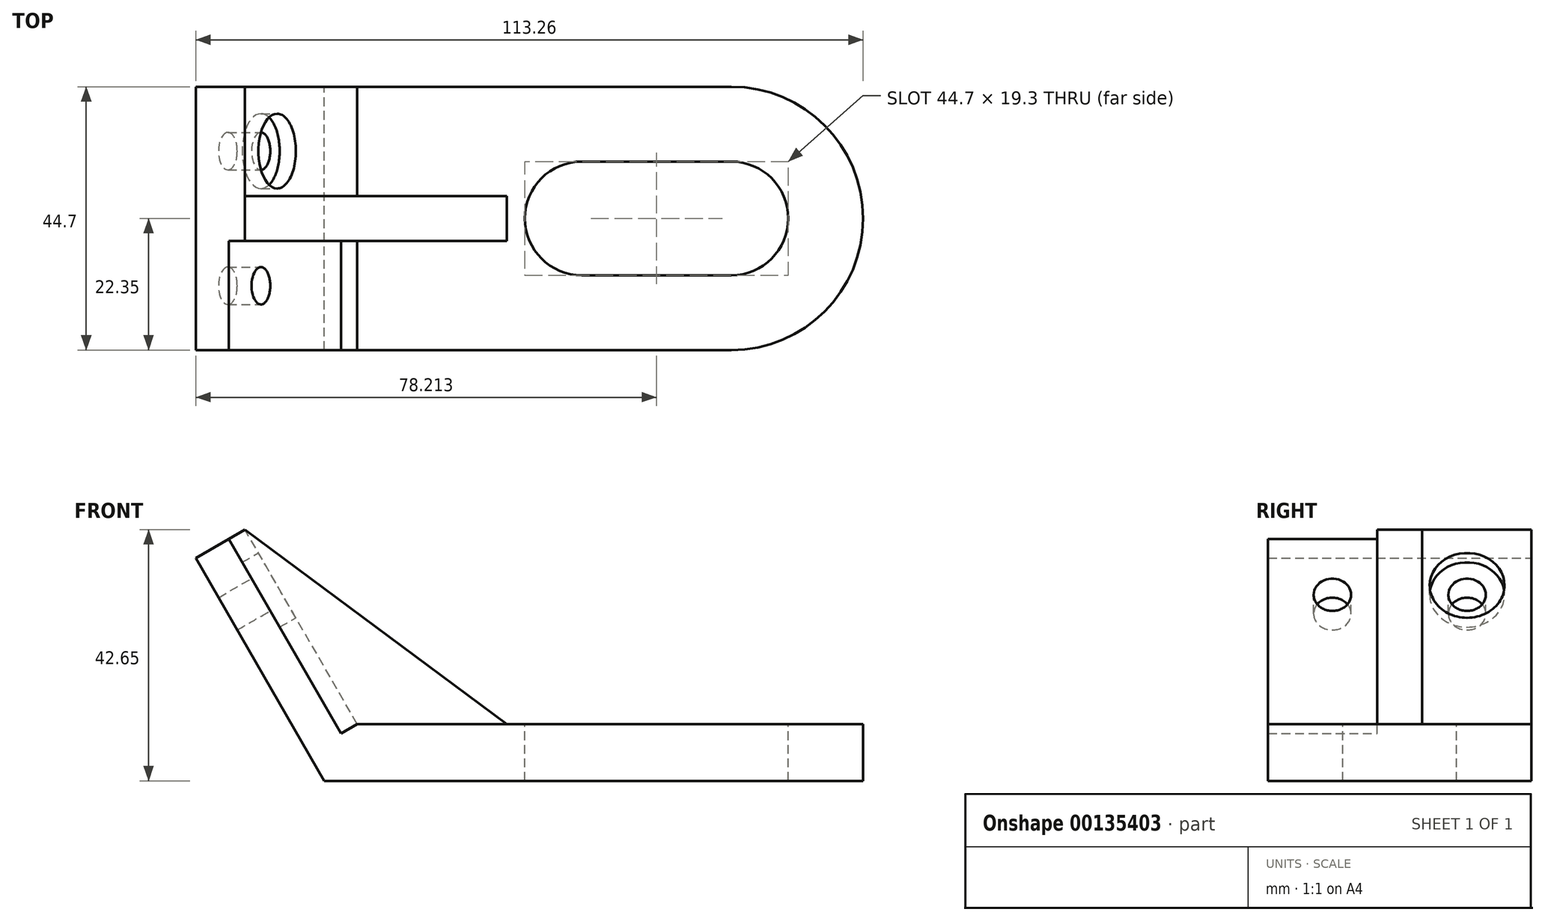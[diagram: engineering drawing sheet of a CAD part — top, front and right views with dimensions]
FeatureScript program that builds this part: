
annotation { "Feature Type Name" : "Feature", "Feature Type Description" : "" }
export const myFeature = defineFeature(function(context is Context, id is Id, definition is map)
    precondition{}
    {
        {
            var Q0;
            Q0=qCreatedBy(makeId("Front.planeOp"),FACE);
            var sketch = newSketch(context, id + "F0", { "sketchPlane" : qUnion([Q0])});
            skLineSegment(sketch, "E0", {"start": v(-21.84, 37.82) * mm, "end": v(0, 0) * mm});
            skLineSegment(sketch, "E1", {"start": v(0, 0) * mm, "end": v(91.42, 0) * mm});
            skLineSegment(sketch, "E2", {"start": v(91.42, 0) * mm, "end": v(91.42, 9.65) * mm});
            skLineSegment(sketch, "E3", {"start": v(91.42, 9.65) * mm, "end": v(5.57, 9.65) * mm});
            skLineSegment(sketch, "E4", {"start": v(5.57, 9.65) * mm, "end": v(-13.48, 42.65) * mm});
            skLineSegment(sketch, "E5", {"start": v(-13.48, 42.65) * mm, "end": v(-21.84, 37.82) * mm});
            skLineSegment(sketch, "E6", {"start": v(-13.48, 42.65) * mm, "end": v(30.97, 9.65) * mm});
            skLineSegment(sketch, "E7", {"start": v(-21.84, 37.82) * mm, "end": v(-21.84, 0) * mm, "construction": true});
            skSolve(sketch);
        }
        {
            var Q0;
            Q0=makeQuery(id+"F0.imprint","IMPRINT",FACE,{"disambiguationData":[TD([[makeQuery(id+"F0.imprint","IMPRINT",EDGE,{"derivedFrom":sQuery(id+"F0.wireOp",EDGE,"E0")}),1.0]])]});
            extrude(context, id + "F1", {"entities" : qUnion([Q0]), "endBound" : BoundingType.SYMMETRIC, "depth" : 44.7 * mm});
        }
        {
            var Q0;
            {var subQ0=sQuery(id+"F0.wireOp",EDGE,"E4");Q0=makeQuery(id+"F0.imprint","IMPRINT",FACE,{"disambiguationData":[TD([[makeQuery(id+"F0.imprint","IMPRINT",EDGE,{"derivedFrom":subQ0}),-1.0]])]});}
            extrude(context, id + "F2", {"entities" : qUnion([Q0]), "operationType" : NewBodyOperationType.ADD, "endBound" : BoundingType.SYMMETRIC, "depth" : 7.62 * mm});
        }
        {
            var Q0;
            Q0=makeQuery(id+"F1.opExtrude","SWEPT_FACE",FACE,{"disambiguationData":[OSD([sQuery(id+"F0.wireOp",EDGE,"E3")])]});
            var sketch = newSketch(context, id + "F3", { "sketchPlane" : qUnion([Q0])});
            skArc(sketch, "E8", {"start": v(43.67, 9.65) * mm, "mid": v(34.02, 0) * mm, "end": v(43.67, -9.65) * mm});
            skArc(sketch, "E9", {"start": v(69.07, -9.65) * mm, "mid": v(78.72, 0) * mm, "end": v(69.07, 9.65) * mm});
            skLineSegment(sketch, "E10", {"start": v(43.67, -9.65) * mm, "end": v(69.07, -9.65) * mm});
            skLineSegment(sketch, "E11", {"start": v(43.67, 9.65) * mm, "end": v(69.07, 9.65) * mm});
            skArc(sketch, "E12", {"start": v(69.07, -22.35) * mm, "mid": v(91.42, 0) * mm, "end": v(69.07, 22.35) * mm});
            skLineSegment(sketch, "E13", {"start": v(69.07, 22.35) * mm, "end": v(69.07, -22.35) * mm});
            skSolve(sketch);
        }
        {
            var Q0;
            Q0=makeQuery(id+"F3.imprint","IMPRINT",FACE,{"disambiguationData":[TD([[makeQuery(id+"F3.imprint","IMPRINT",EDGE,{"derivedFrom":sQuery(id+"F3.wireOp",EDGE,"E8")}),1.0]])]});
            var Q1;
            {var subQ0=sQuery(id+"F3.wireOp",EDGE,"E9");Q1=makeQuery(id+"F3.imprint","IMPRINT",FACE,{"disambiguationData":[TD([[makeQuery(id+"F3.imprint","IMPRINT",EDGE,{"derivedFrom":subQ0}),1.0]])]});}
            var Q2;
            {var subQ0=sQuery(id+"F3.wireOp",EDGE,"E12");var subQ1=sQuery(id+"F0.wireOp",EDGE,"E3");var subQ2=makeQuery(id+"F1.opExtrude","CAP_EDGE",EDGE,{"disambiguationData":[OSD([subQ1])],"isStart":true});var subQ3=makeQuery(id+"F3.imprint","INTERSECT",VERTEX,{"derivedFrom":[subQ2,subQ0,sQuery(id+"F3.wireOp",EDGE,"E13")]});Q2=makeQuery(id+"F3.imprint","IMPRINT",FACE,{"disambiguationData":[TD([[makeQuery(id+"F3.imprint","IMPRINT",EDGE,{"disambiguationData":[TD([[subQ3,1.0]])],"derivedFrom":subQ0}),-1.0]])]});}
            var Q3;
            {var subQ0=sQuery(id+"F3.wireOp",EDGE,"E12");var subQ1=sQuery(id+"F0.wireOp",EDGE,"E3");var subQ2=makeQuery(id+"F1.opExtrude","CAP_EDGE",EDGE,{"disambiguationData":[OSD([subQ1])],"isStart":false});var subQ3=makeQuery(id+"F3.imprint","INTERSECT",VERTEX,{"derivedFrom":[subQ2,subQ0,sQuery(id+"F3.wireOp",EDGE,"E13")]});Q3=makeQuery(id+"F3.imprint","IMPRINT",FACE,{"disambiguationData":[TD([[makeQuery(id+"F3.imprint","IMPRINT",EDGE,{"disambiguationData":[TD([[subQ3,-1.0]])],"derivedFrom":subQ0}),-1.0]])]});}
            extrude(context, id + "F4", {"entities" : qUnion([Q0, Q1, Q2, Q3]), "operationType" : NewBodyOperationType.REMOVE, "oppositeDirection" : true, "depth" : 9.65 * mm});
        }
        {
            var Q0;
            {var subQ0=sQuery(id+"F0.wireOp",EDGE,"E6");var subQ1=sQuery(id+"F0.wireOp",EDGE,"E4");var subQ2=sQuery(id+"F0.wireOp",EDGE,"E3");Q0=makeQuery(id+"F2.boolean.opBoolean","SPLIT",FACE,{"disambiguationData":[TD([makeQuery(id+"F2.opExtrude","CAP_FACE",FACE,{"disambiguationData":[OSD([subQ2,subQ1,subQ0])],"isStart":false})])],"derivedFrom":makeQuery(id+"F1.opExtrude","SWEPT_FACE",FACE,{"disambiguationData":[OSD([subQ1])]})});}
            var sketch = newSketch(context, id + "F5", { "sketchPlane" : qUnion([Q0])});
            skCircle(sketch, "E14", {"center": v(11.43, 32.75) * mm, "radius": 6.35 * mm});
            skCircle(sketch, "E15", {"center": v(11.43, 32.75) * mm, "radius": 3.18 * mm});
            skCircle(sketch, "E16.MirrorC", {"center": v(-11.43, 32.75) * mm, "radius": 6.35 * mm});
            skCircle(sketch, "E17.MirrorC", {"center": v(-11.43, 32.75) * mm, "radius": 3.18 * mm});
            skSolve(sketch);
        }
        {
            var Q0;
            Q0=makeQuery(id+"F5.imprint","IMPRINT",FACE,{"disambiguationData":[TD([[makeQuery(id+"F5.imprint","IMPRINT",EDGE,{"derivedFrom":sQuery(id+"F5.wireOp",EDGE,"E16.MirrorC")}),-1.0]])]});
            extrude(context, id + "F6", {"entities" : qUnion([Q0]), "operationType" : NewBodyOperationType.REMOVE, "oppositeDirection" : true, "depth" : 3.17 * mm});
        }
        {
            var Q0;
            Q0 = qSketchRegion(id + "F5", true);
            extrude(context, id + "F7", {"entities" : qUnion([Q0]), "operationType" : NewBodyOperationType.REMOVE, "oppositeDirection" : true, "depth" : 3.17 * mm});
        }
        {
            var Q0;
            {var subQ0=sQuery(id+"F0.wireOp",EDGE,"E6");var subQ1=sQuery(id+"F0.wireOp",EDGE,"E4");var subQ2=sQuery(id+"F0.wireOp",EDGE,"E3");Q0=makeQuery(id+"F6.boolean.opBoolean","SPLIT",FACE,{"disambiguationData":[TD([makeQuery(id+"F6.opExtrude","SWEPT_FACE",FACE,{"disambiguationData":[OSD([sQuery(id+"F5.wireOp",EDGE,"E17.MirrorC")])]})])],"derivedFrom":makeQuery(id+"F2.boolean.opBoolean","SPLIT",FACE,{"disambiguationData":[TD([makeQuery(id+"F2.opExtrude","CAP_FACE",FACE,{"disambiguationData":[OSD([subQ2,subQ1,subQ0])],"isStart":false})])],"derivedFrom":makeQuery(id+"F1.opExtrude","SWEPT_FACE",FACE,{"disambiguationData":[OSD([subQ1])]})})});}
            var Q1;
            {var subQ1=sQuery(id+"F0.wireOp",EDGE,"E6");var subQ2=sQuery(id+"F0.wireOp",EDGE,"E4");var subQ3=sQuery(id+"F0.wireOp",EDGE,"E3");Q1=makeQuery(id+"F7.boolean.opBoolean","SPLIT",FACE,{"disambiguationData":[TD([makeQuery(id+"F7.opExtrude","SWEPT_FACE",FACE,{"disambiguationData":[OSD([sQuery(id+"F5.wireOp",EDGE,"E15")])]})])],"derivedFrom":makeQuery(id+"F2.boolean.opBoolean","SPLIT",FACE,{"disambiguationData":[TD([makeQuery(id+"F2.opExtrude","CAP_FACE",FACE,{"disambiguationData":[OSD([subQ3,subQ2,subQ1])],"isStart":true})])],"derivedFrom":makeQuery(id+"F1.opExtrude","SWEPT_FACE",FACE,{"disambiguationData":[OSD([subQ2])]})})});}
            extrude(context, id + "F8", {"entities" : qUnion([Q0, Q1]), "operationType" : NewBodyOperationType.REMOVE, "oppositeDirection" : true, "depth" : 25.4 * mm});
        }
    });
